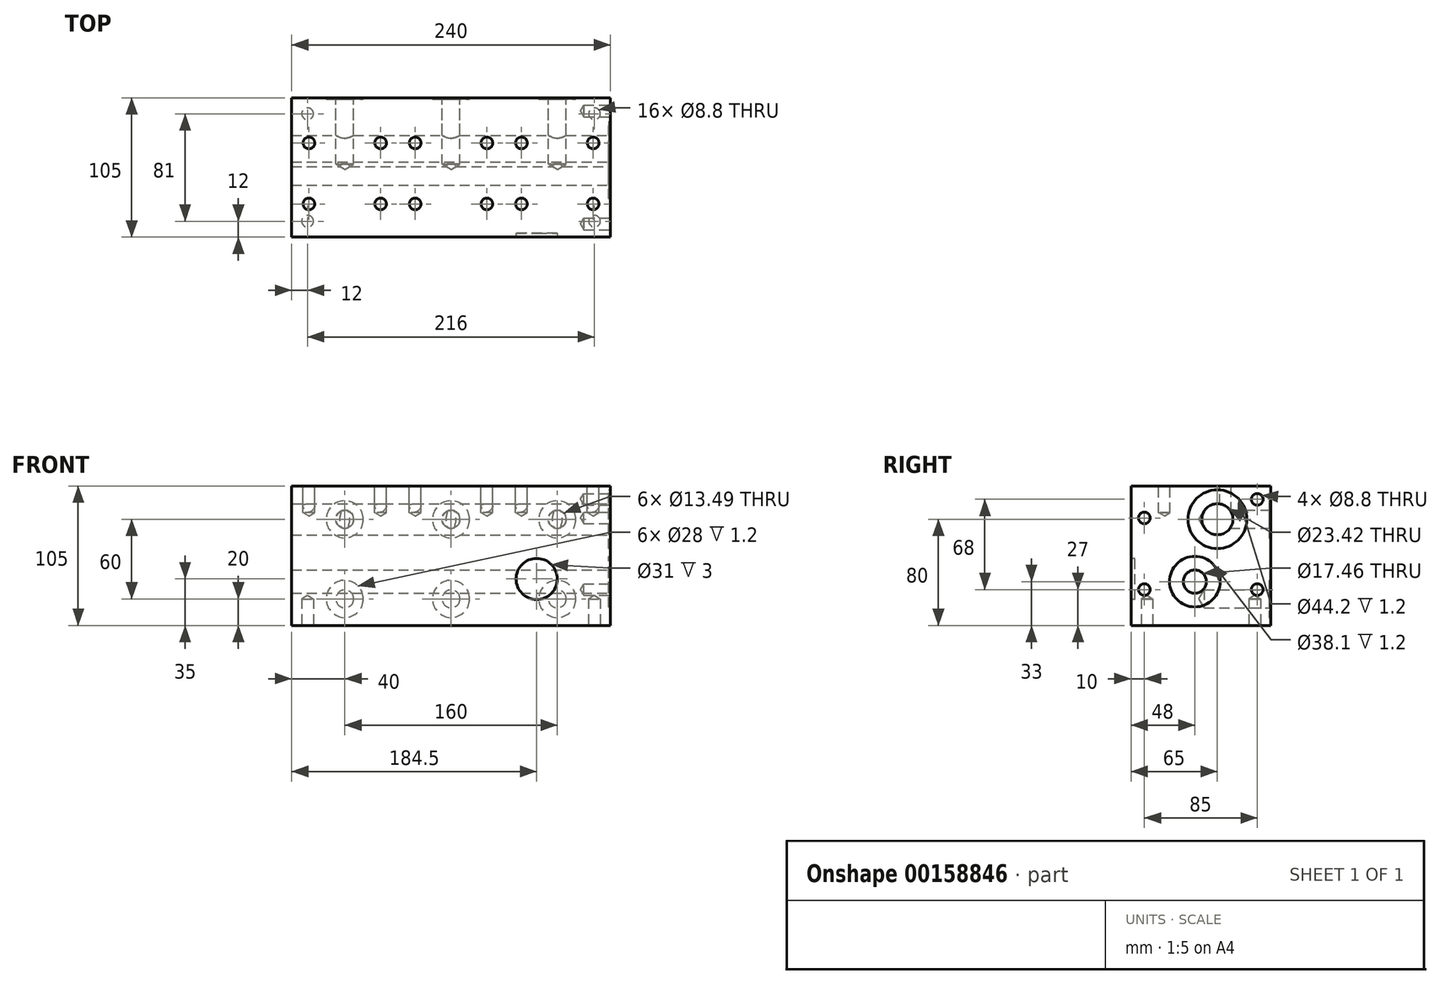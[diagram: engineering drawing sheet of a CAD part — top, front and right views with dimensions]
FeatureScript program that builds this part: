
annotation { "Feature Type Name" : "Feature", "Feature Type Description" : "" }
export const myFeature = defineFeature(function(context is Context, id is Id, definition is map)
    precondition{}
    {
        {
            var Q0;
            Q0=qCreatedBy(makeId("Right.planeOp"),FACE);
            var sketch = newSketch(context, id + "F0", { "sketchPlane" : qUnion([Q0])});
            skLineSegment(sketch, "E0.bottom", {"start": v(-52.5, -52.5) * mm, "end": v(52.5, -52.5) * mm});
            skLineSegment(sketch, "E0.top", {"start": v(-52.5, 52.5) * mm, "end": v(52.5, 52.5) * mm});
            skLineSegment(sketch, "E0.left", {"start": v(-52.5, -52.5) * mm, "end": v(-52.5, 52.5) * mm});
            skLineSegment(sketch, "E0.right", {"start": v(52.5, -52.5) * mm, "end": v(52.5, 52.5) * mm});
            skPoint(sketch, "E0.middle", {"position": v(0, 0) * mm});
            skSolve(sketch);
        }
        {
            var Q0;
            Q0=qSketchRegion(id+"F0",true);
            extrude(context, id + "F1", {"entities" : qUnion([Q0]), "depth" : 240 * mm});
        }
        {
            var Q0;
            Q0=makeQuery(id+"F1.opExtrude","CAP_FACE",FACE,{"disambiguationData":[OSD([sQuery(id+"F0.wireOp",EDGE,"E0.bottom"),sQuery(id+"F0.wireOp",EDGE,"E0.top"),sQuery(id+"F0.wireOp",EDGE,"E0.left"),sQuery(id+"F0.wireOp",EDGE,"E0.right")])],"isStart":false});
            var sketch = newSketch(context, id + "F2", { "sketchPlane" : qUnion([Q0])});
            skPoint(sketch, "E1", {"position": v(12.5, 27.5) * mm});
            skPoint(sketch, "E2", {"position": v(-4.5, -19.5) * mm});
            skPoint(sketch, "E3", {"position": v(-42.5, -25.5) * mm});
            skPoint(sketch, "E4", {"position": v(-42.5, 28.5) * mm});
            skPoint(sketch, "E5", {"position": v(42.5, -25.5) * mm});
            skPoint(sketch, "E6", {"position": v(42.5, 42.5) * mm});
            skCircle(sketch, "E7", {"center": v(-4.5, -19.5) * mm, "radius": 19.05 * mm});
            skCircle(sketch, "E8", {"center": v(12.5, 27.5) * mm, "radius": 22.1 * mm});
            skSolve(sketch);
        }
        {
            var Q0;
            Q0=sQuery(id+"F2.wireOp",VERTEX,"E4");
            var Q1;
            Q1=sQuery(id+"F2.wireOp",VERTEX,"E6");
            var Q2;
            Q2=sQuery(id+"F2.wireOp",VERTEX,"E5");
            var Q3;
            Q3=sQuery(id+"F2.wireOp",VERTEX,"E3");
            var Q4;
            Q4=makeQuery(id+"F1.opExtrude","SWEPT_BODY",BODY,{"disambiguationData":[OSD([sQuery(id+"F0.wireOp",EDGE,"E0.bottom"),sQuery(id+"F0.wireOp",EDGE,"E0.top"),sQuery(id+"F0.wireOp",EDGE,"E0.left"),sQuery(id+"F0.wireOp",EDGE,"E0.right")])]});
            hole(context, id + "F3", {"style" : HoleStyle.SIMPLE, "endStyle" : HoleEndStyle.BLIND, "standardTappedOrClearance" : lookupTablePath({ "standard" : "ISO", "engagement" : "75%", "pitch" : "1.25 mm", "size" : "M10", "type" : "Tapped" }), "standardBlindInLast" : lookupTablePath({ "standard" : "ISO", "engagement" : "75%", "pitch" : "1.25 mm", "size" : "M10", "type" : "Tapped" }), "holeDiameter" : 8.8 * mm, "holeDepth" : 20 * mm, "locations" : qUnion([Q0, Q1, Q2, Q3]), "scope" : qUnion([Q4]), "majorDiameter" : 10 * mm});
        }
        {
            var Q0;
            Q0=sQuery(id+"F2.wireOp",VERTEX,"E2");
            var Q1;
            Q1=makeQuery(id+"F1.opExtrude","SWEPT_BODY",BODY,{"disambiguationData":[OSD([sQuery(id+"F0.wireOp",EDGE,"E0.bottom"),sQuery(id+"F0.wireOp",EDGE,"E0.top"),sQuery(id+"F0.wireOp",EDGE,"E0.left"),sQuery(id+"F0.wireOp",EDGE,"E0.right")])]});
            hole(context, id + "F4", {"style" : HoleStyle.SIMPLE, "endStyle" : HoleEndStyle.THROUGH, "standardTappedOrClearance" : lookupTablePath({ "standard" : "ANSI", "engagement" : "75%", "pitch" : "16 tpi", "size" : "3/4", "type" : "Tapped" }), "standardBlindInLast" : lookupTablePath({ "standard" : "ANSI", "engagement" : "75%", "pitch" : "16 tpi", "size" : "3/4", "type" : "Tapped" }), "holeDiameter" : 17.46 * mm, "locations" : qUnion([Q0]), "scope" : qUnion([Q1]), "isTappedThrough" : true, "majorDiameter" : 19.05 * mm, "showTappedDepth" : true});
        }
        {
            var Q0;
            Q0=sQuery(id+"F2.wireOp",VERTEX,"E1");
            var Q1;
            Q1=makeQuery(id+"F1.opExtrude","SWEPT_BODY",BODY,{"disambiguationData":[OSD([sQuery(id+"F0.wireOp",EDGE,"E0.bottom"),sQuery(id+"F0.wireOp",EDGE,"E0.top"),sQuery(id+"F0.wireOp",EDGE,"E0.left"),sQuery(id+"F0.wireOp",EDGE,"E0.right")])]});
            hole(context, id + "F5", {"style" : HoleStyle.SIMPLE, "endStyle" : HoleEndStyle.THROUGH, "standardTappedOrClearance" : lookupTablePath({ "standard" : "ANSI", "engagement" : "75%", "pitch" : "12 tpi", "size" : "1", "type" : "Tapped" }), "standardBlindInLast" : lookupTablePath({ "standard" : "ANSI", "engagement" : "75%", "pitch" : "12 tpi", "size" : "1", "type" : "Tapped" }), "holeDiameter" : 23.42 * mm, "locations" : qUnion([Q0]), "scope" : qUnion([Q1]), "isTappedThrough" : true, "majorDiameter" : 25.4 * mm, "showTappedDepth" : true});
        }
        {
            var Q0;
            Q0=qSketchRegion(id+"F2",true);
            extrude(context, id + "F6", {"entities" : qUnion([Q0]), "operationType" : NewBodyOperationType.REMOVE, "oppositeDirection" : true, "depth" : 1.2 * mm});
        }
        {
            var Q0;
            Q0=makeQuery(id+"F1.opExtrude","SWEPT_FACE",FACE,{"disambiguationData":[OSD([sQuery(id+"F0.wireOp",EDGE,"E0.right")])]});
            var sketch = newSketch(context, id + "F7", { "sketchPlane" : qUnion([Q0])});
            skPoint(sketch, "E9", {"position": v(-200, 27.5) * mm});
            skPoint(sketch, "E10", {"position": v(-200, -32.5) * mm});
            skPoint(sketch, "E11.1.0.0", {"position": v(-120, 27.5) * mm});
            skPoint(sketch, "E11.1.0.1", {"position": v(-120, -32.5) * mm});
            skPoint(sketch, "E11.2.0.0", {"position": v(-40, 27.5) * mm});
            skPoint(sketch, "E11.2.0.1", {"position": v(-40, -32.5) * mm});
            skPoint(sketch, "E11.3.0.0", {"position": v(40, 27.5) * mm});
            skPoint(sketch, "E11.3.0.1", {"position": v(40, -32.5) * mm});
            skPoint(sketch, "E11.4.0.0", {"position": v(120, 27.5) * mm});
            skPoint(sketch, "E11.4.0.1", {"position": v(120, -32.5) * mm});
            skPoint(sketch, "E11.5.0.0", {"position": v(200, 27.5) * mm});
            skPoint(sketch, "E11.5.0.1", {"position": v(200, -32.5) * mm});
            skPoint(sketch, "E11.6.0.0", {"position": v(280, 27.5) * mm});
            skPoint(sketch, "E11.6.0.1", {"position": v(280, -32.5) * mm});
            skLineSegment(sketch, "E11.direction1", {"start": v(-200, 27.5) * mm, "end": v(-120, 27.5) * mm, "construction": true});
            skCircle(sketch, "E12", {"center": v(-200, 27.5) * mm, "radius": 14 * mm});
            skCircle(sketch, "E13.0.1.0", {"center": v(-200, -32.5) * mm, "radius": 14 * mm});
            skCircle(sketch, "E13.1.0.0", {"center": v(-120, 27.5) * mm, "radius": 14 * mm});
            skCircle(sketch, "E13.1.1.0", {"center": v(-120, -32.5) * mm, "radius": 14 * mm});
            skCircle(sketch, "E13.2.0.0", {"center": v(-40, 27.5) * mm, "radius": 14 * mm});
            skCircle(sketch, "E13.2.1.0", {"center": v(-40, -32.5) * mm, "radius": 14 * mm});
            skCircle(sketch, "E13.3.0.0", {"center": v(40, 27.5) * mm, "radius": 14 * mm});
            skCircle(sketch, "E13.3.1.0", {"center": v(40, -32.5) * mm, "radius": 14 * mm});
            skCircle(sketch, "E13.4.0.0", {"center": v(120, 27.5) * mm, "radius": 14 * mm});
            skCircle(sketch, "E13.4.1.0", {"center": v(120, -32.5) * mm, "radius": 14 * mm});
            skCircle(sketch, "E13.5.0.0", {"center": v(200, 27.5) * mm, "radius": 14 * mm});
            skCircle(sketch, "E13.5.1.0", {"center": v(200, -32.5) * mm, "radius": 14 * mm});
            skCircle(sketch, "E13.6.0.0", {"center": v(280, 27.5) * mm, "radius": 14 * mm});
            skCircle(sketch, "E13.6.1.0", {"center": v(280, -32.5) * mm, "radius": 14 * mm});
            skLineSegment(sketch, "E13.direction2", {"start": v(-200, 27.5) * mm, "end": v(-200, -32.5) * mm, "construction": true});
            skSolve(sketch);
        }
        {
            var Q0;
            Q0=sQuery(id+"F7.wireOp",VERTEX,"E9");
            var Q1;
            Q1=sQuery(id+"F7.wireOp",VERTEX,"E10");
            var Q2;
            Q2=sQuery(id+"F7.wireOp",VERTEX,"E11.1.0.1");
            var Q3;
            Q3=sQuery(id+"F7.wireOp",VERTEX,"E11.1.0.0");
            var Q4;
            Q4=sQuery(id+"F7.wireOp",VERTEX,"E11.2.0.0");
            var Q5;
            Q5=sQuery(id+"F7.wireOp",VERTEX,"E11.2.0.1");
            var Q6;
            Q6=sQuery(id+"F7.wireOp",VERTEX,"E11.3.0.1");
            var Q7;
            Q7=sQuery(id+"F7.wireOp",VERTEX,"E11.3.0.0");
            var Q8;
            Q8=sQuery(id+"F7.wireOp",VERTEX,"E11.4.0.0");
            var Q9;
            Q9=sQuery(id+"F7.wireOp",VERTEX,"E11.4.0.1");
            var Q10;
            Q10=sQuery(id+"F7.wireOp",VERTEX,"E11.5.0.1");
            var Q11;
            Q11=sQuery(id+"F7.wireOp",VERTEX,"E11.5.0.0");
            var Q12;
            Q12=sQuery(id+"F7.wireOp",VERTEX,"E11.6.0.0");
            var Q13;
            Q13=sQuery(id+"F7.wireOp",VERTEX,"E11.6.0.1");
            var Q14;
            Q14=makeQuery(id+"F1.opExtrude","SWEPT_BODY",BODY,{"disambiguationData":[OSD([sQuery(id+"F0.wireOp",EDGE,"E0.bottom"),sQuery(id+"F0.wireOp",EDGE,"E0.top"),sQuery(id+"F0.wireOp",EDGE,"E0.left"),sQuery(id+"F0.wireOp",EDGE,"E0.right")])]});
            hole(context, id + "F8", {"style" : HoleStyle.SIMPLE, "endStyle" : HoleEndStyle.BLIND, "standardTappedOrClearance" : lookupTablePath({ "standard" : "ANSI", "fit" : "Normal (ASME)", "size" : "1/2", "type" : "Clearance" }), "standardBlindInLast" : lookupTablePath({ "fit" : "Free", "standard" : "ANSI", "size" : "1/2", "type" : "Clearance" }), "holeDiameter" : 13.5 * mm, "holeDepth" : 50 * mm, "locations" : qUnion([Q0, Q1, Q2, Q3, Q4, Q5, Q6, Q7, Q8, Q9, Q10, Q11, Q12, Q13]), "scope" : qUnion([Q14])});
        }
        {
            var Q0;
            Q0=qSketchRegion(id+"F7",true);
            extrude(context, id + "F9", {"entities" : qUnion([Q0]), "operationType" : NewBodyOperationType.REMOVE, "oppositeDirection" : true, "depth" : 1.2 * mm});
        }
        {
            var Q0;
            Q0=makeQuery(id+"F1.opExtrude","SWEPT_FACE",FACE,{"disambiguationData":[OSD([sQuery(id+"F0.wireOp",EDGE,"E0.top")])]});
            var sketch = newSketch(context, id + "F10", { "sketchPlane" : qUnion([Q0])});
            skPoint(sketch, "E14", {"position": v(13, 18.5) * mm});
            skPoint(sketch, "E15", {"position": v(67, 18.5) * mm});
            skPoint(sketch, "E16", {"position": v(13, -27.5) * mm});
            skPoint(sketch, "E17", {"position": v(67, -27.5) * mm});
            skPoint(sketch, "E18.1.0.0", {"position": v(93, 18.5) * mm});
            skPoint(sketch, "E18.1.0.1", {"position": v(93, -27.5) * mm});
            skPoint(sketch, "E18.1.0.2", {"position": v(147, -27.5) * mm});
            skPoint(sketch, "E18.1.0.3", {"position": v(147, 18.5) * mm});
            skPoint(sketch, "E18.2.0.0", {"position": v(173, 18.5) * mm});
            skPoint(sketch, "E18.2.0.1", {"position": v(173, -27.5) * mm});
            skPoint(sketch, "E18.2.0.2", {"position": v(227, -27.5) * mm});
            skPoint(sketch, "E18.2.0.3", {"position": v(227, 18.5) * mm});
            skLineSegment(sketch, "E18.direction1", {"start": v(13, 18.5) * mm, "end": v(93, 18.5) * mm, "construction": true});
            skSolve(sketch);
        }
        {
            var Q0;
            Q0=sQuery(id+"F10.wireOp",VERTEX,"E14");
            var Q1;
            Q1=sQuery(id+"F10.wireOp",VERTEX,"E16");
            var Q2;
            Q2=sQuery(id+"F10.wireOp",VERTEX,"E17");
            var Q3;
            Q3=sQuery(id+"F10.wireOp",VERTEX,"E15");
            var Q4;
            Q4=sQuery(id+"F10.wireOp",VERTEX,"E18.1.0.0");
            var Q5;
            Q5=sQuery(id+"F10.wireOp",VERTEX,"E18.1.0.1");
            var Q6;
            Q6=sQuery(id+"F10.wireOp",VERTEX,"E18.1.0.3");
            var Q7;
            Q7=sQuery(id+"F10.wireOp",VERTEX,"E18.1.0.2");
            var Q8;
            Q8=sQuery(id+"F10.wireOp",VERTEX,"E18.2.0.1");
            var Q9;
            Q9=sQuery(id+"F10.wireOp",VERTEX,"E18.2.0.0");
            var Q10;
            Q10=sQuery(id+"F10.wireOp",VERTEX,"E18.2.0.3");
            var Q11;
            Q11=sQuery(id+"F10.wireOp",VERTEX,"E18.2.0.2");
            var Q12;
            Q12=sQuery(id+"F10.wireOp",VERTEX,"E18.3.0.1");
            var Q13;
            Q13=sQuery(id+"F10.wireOp",VERTEX,"E18.3.0.0");
            var Q14;
            Q14=sQuery(id+"F10.wireOp",VERTEX,"E18.3.0.3");
            var Q15;
            Q15=sQuery(id+"F10.wireOp",VERTEX,"E18.3.0.2");
            var Q16;
            Q16=sQuery(id+"F10.wireOp",VERTEX,"E18.4.0.1");
            var Q17;
            Q17=sQuery(id+"F10.wireOp",VERTEX,"E18.4.0.0");
            var Q18;
            Q18=sQuery(id+"F10.wireOp",VERTEX,"E18.4.0.3");
            var Q19;
            Q19=sQuery(id+"F10.wireOp",VERTEX,"E18.4.0.2");
            var Q20;
            Q20=sQuery(id+"F10.wireOp",VERTEX,"E18.5.0.1");
            var Q21;
            Q21=sQuery(id+"F10.wireOp",VERTEX,"E18.5.0.0");
            var Q22;
            Q22=sQuery(id+"F10.wireOp",VERTEX,"E18.5.0.3");
            var Q23;
            Q23=sQuery(id+"F10.wireOp",VERTEX,"E18.6.0.0");
            var Q24;
            Q24=sQuery(id+"F10.wireOp",VERTEX,"E18.5.0.2");
            var Q25;
            Q25=sQuery(id+"F10.wireOp",VERTEX,"E18.6.0.1");
            var Q26;
            Q26=sQuery(id+"F10.wireOp",VERTEX,"E18.6.0.3");
            var Q27;
            Q27=sQuery(id+"F10.wireOp",VERTEX,"E18.6.0.2");
            var Q28;
            Q28=makeQuery(id+"F1.opExtrude","SWEPT_BODY",BODY,{"disambiguationData":[OSD([sQuery(id+"F0.wireOp",EDGE,"E0.bottom"),sQuery(id+"F0.wireOp",EDGE,"E0.top"),sQuery(id+"F0.wireOp",EDGE,"E0.left"),sQuery(id+"F0.wireOp",EDGE,"E0.right")])]});
            hole(context, id + "F11", {"style" : HoleStyle.SIMPLE, "endStyle" : HoleEndStyle.BLIND, "standardTappedOrClearance" : lookupTablePath({ "standard" : "ISO", "engagement" : "75%", "pitch" : "1.25 mm", "size" : "M10", "type" : "Tapped" }), "standardBlindInLast" : lookupTablePath({ "standard" : "ISO", "engagement" : "75%", "pitch" : "1.25 mm", "size" : "M10", "type" : "Tapped" }), "holeDiameter" : 8.8 * mm, "holeDepth" : 20 * mm, "locations" : qUnion([Q0, Q1, Q2, Q3, Q4, Q5, Q6, Q7, Q8, Q9, Q10, Q11, Q12, Q13, Q14, Q15, Q16, Q17, Q18, Q19, Q20, Q21, Q22, Q23, Q24, Q25, Q26, Q27]), "scope" : qUnion([Q28]), "majorDiameter" : 10 * mm});
        }
        {
            var Q0;
            Q0=makeQuery(id+"F1.opExtrude","SWEPT_FACE",FACE,{"disambiguationData":[OSD([sQuery(id+"F0.wireOp",EDGE,"E0.bottom")])]});
            var sketch = newSketch(context, id + "F12", { "sketchPlane" : qUnion([Q0])});
            skPoint(sketch, "E19", {"position": v(12, 40.5) * mm});
            skPoint(sketch, "E20", {"position": v(12, -40.5) * mm});
            skPoint(sketch, "E21", {"position": v(228, 40.5) * mm});
            skPoint(sketch, "E22", {"position": v(228, -40.5) * mm});
            skSolve(sketch);
        }
        {
            var Q0;
            Q0=sQuery(id+"F12.wireOp",VERTEX,"E19");
            var Q1;
            Q1=sQuery(id+"F12.wireOp",VERTEX,"E20");
            var Q2;
            Q2=sQuery(id+"F12.wireOp",VERTEX,"E22");
            var Q3;
            Q3=sQuery(id+"F12.wireOp",VERTEX,"E21");
            var Q4;
            Q4=makeQuery(id+"F1.opExtrude","SWEPT_BODY",BODY,{"disambiguationData":[OSD([sQuery(id+"F0.wireOp",EDGE,"E0.bottom"),sQuery(id+"F0.wireOp",EDGE,"E0.top"),sQuery(id+"F0.wireOp",EDGE,"E0.left"),sQuery(id+"F0.wireOp",EDGE,"E0.right")])]});
            hole(context, id + "F13", {"style" : HoleStyle.SIMPLE, "endStyle" : HoleEndStyle.BLIND, "standardTappedOrClearance" : lookupTablePath({ "standard" : "ISO", "fit" : "Normal", "size" : "M8", "type" : "Clearance" }), "standardBlindInLast" : lookupTablePath({ "fit" : "Standard", "standard" : "ISO", "size" : "M8", "type" : "Clearance" }), "holeDiameter" : 8.8 * mm, "holeDepth" : 20 * mm, "locations" : qUnion([Q0, Q1, Q2, Q3]), "scope" : qUnion([Q4])});
        }
        {
            var Q0;
            Q0=makeQuery(id+"F1.opExtrude","SWEPT_FACE",FACE,{"disambiguationData":[OSD([sQuery(id+"F0.wireOp",EDGE,"E0.left")])]});
            var sketch = newSketch(context, id + "F14", { "sketchPlane" : qUnion([Q0])});
            skCircle(sketch, "E23", {"center": v(184.5, -17.5) * mm, "radius": 15.5 * mm});
            skSolve(sketch);
        }
        {
            var Q0;
            Q0=qSketchRegion(id+"F14",true);
            extrude(context, id + "F15", {"entities" : qUnion([Q0]), "operationType" : NewBodyOperationType.REMOVE, "oppositeDirection" : true, "depth" : 3 * mm});
        }
    });
